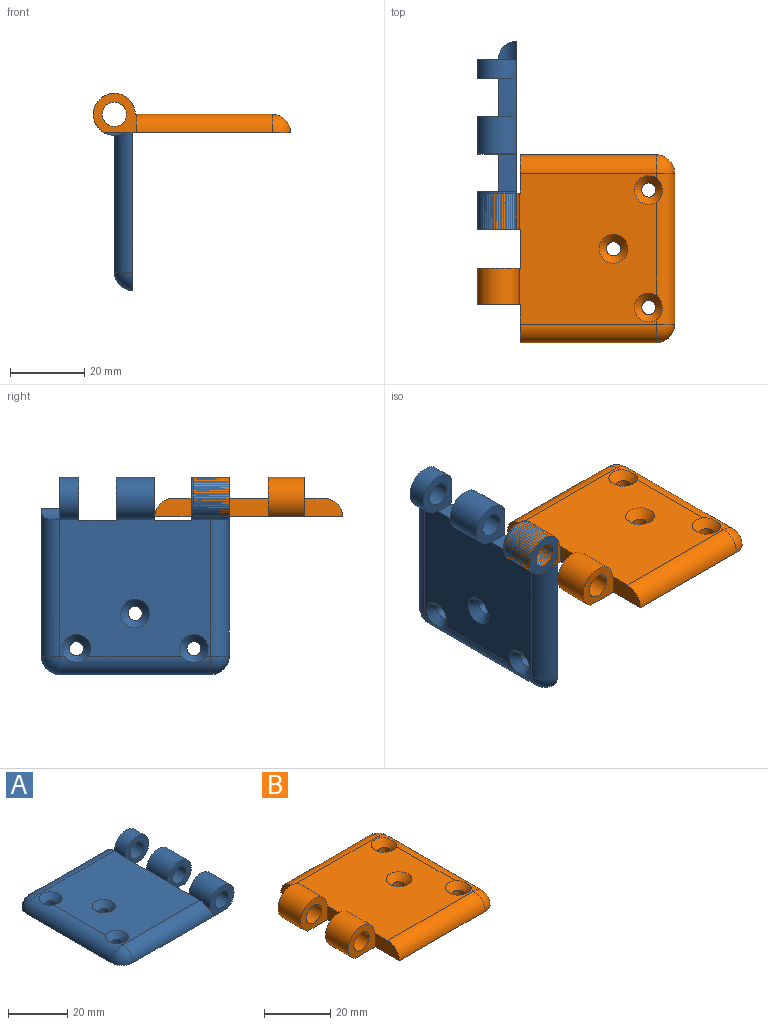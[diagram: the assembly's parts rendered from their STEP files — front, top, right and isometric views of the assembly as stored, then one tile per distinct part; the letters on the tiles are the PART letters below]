
ASSEMBLY  parts=2 mates=1
PART A: 28 faces, bbox 53.3x50.8x10.7 mm
  f0: plane 50.8x50.31mm, normal (0,0,-1), area 2310.2mm2, adj f1,f2,f4,f7,f8,f9,f10,f12
  f1: cylinder r=5.68mm len=11.35mm, axis (0,1,0), area 243.3mm2, adj f0,f5,f9,f14
  f2: cylinder r=5.68mm len=11.35mm, axis (0,1,0), area 123.6mm2, adj f0,f5,f10,f27
  f3: cylinder r=3.28mm len=6.55mm, axis (0,1,0), area 106.2mm2, adj f10,f27
  f4: cylinder r=5.68mm len=11.35mm, axis (0,1,0), area 248.9mm2, adj f0,f5,f7,f13,f21
  f5: plane 40.8x36.95mm, normal (0,0,1), area 1378.2mm2, adj f1,f2,f4,f8,f9,f10,f12,f13
  f6: cylinder r=3.28mm len=10.16mm, axis (0,1,0), area 209.1mm2, adj f7,f13
  f7: plane 11.35x10.68mm, normal (0,-1,0), area 65mm2, adj f0,f4,f6
  f8: plane 10.16x5mm, normal (1,0,0), area 50.8mm2, adj f0,f5,f9,f10
  f9: plane 11.55x10.68mm, normal (0,1,0), area 70.3mm2, adj f0,f1,f5,f8,f11
  f10: plane 11.55x10.68mm, normal (0,-1,0), area 70.3mm2, adj f0,f2,f3,f5,f8
  f11: cylinder r=3.28mm len=10.16mm, axis (0,1,0), area 209.1mm2, adj f9,f14
  f12: plane 10.16x5mm, normal (1,0,0), area 50.8mm2, adj f0,f5,f13,f14
  f13: plane 11.55x10.68mm, normal (0,1,0), area 70.3mm2, adj f0,f4,f5,f6,f12
  f14: plane 11.55x10.68mm, normal (0,-1,0), area 70.3mm2, adj f0,f1,f5,f11,f12
  f15: cylinder r=1.9mm len=3.8mm, axis (0,0,1), area 32.2mm2, adj f0,f16
  f16: cone r=1.9mm half-angle=41deg, axis (0,0,1), area 53.9mm2, adj f5,f15,f25
  f17: cylinder r=1.9mm len=3.8mm, axis (0,0,1), area 32.2mm2, adj f0,f18
  f18: cone r=1.9mm half-angle=41deg, axis (0,0,1), area 55.5mm2, adj f5,f17
  f19: cylinder r=1.9mm len=3.8mm, axis (0,0,1), area 32.2mm2, adj f0,f20
  f20: cone r=1.9mm half-angle=41deg, axis (0,0,1), area 53.9mm2, adj f5,f19,f25
  f21: cylinder r=5mm len=39.94mm, axis (1,0,0), area 294.8mm2, adj f0,f4,f5,f23
  f22: cylinder r=5mm len=39.94mm, axis (-1,0,0), area 294.8mm2, adj f0,f5,f24,f26
  f23: sphere r=5mm, area 39.3mm2, adj f0,f21,f25
  f24: sphere r=5mm, area 39.3mm2, adj f0,f22,f25
  f25: cylinder r=5mm len=40.8mm, axis (0,-1,0), area 304.3mm2, adj f0,f5,f16,f20,f23,f24
  f26: cylinder r=5.68mm len=5mm, axis (0,1,0), area 25mm2, adj f0,f22,f27
  f27: plane 11.35x10.68mm, normal (0,1,0), area 65mm2, adj f0,f2,f3,f26
PART B: 24 faces, bbox 53.3x50.8x10.7 mm
  f0: plane 50.8x50.31mm, normal (0,0,-1), area 2243.3mm2, adj f1,f2,f4,f5,f6,f8,f9,f10
  f1: cylinder r=5.68mm len=11.35mm, axis (0,1,0), area 233.7mm2, adj f0,f3,f4,f8
  f2: cylinder r=5.68mm len=11.35mm, axis (0,1,0), area 233.7mm2, adj f0,f3,f5,f10
  f3: plane 40.8x36.95mm, normal (0,0,1), area 1378mm2, adj f1,f2,f4,f5,f6,f8,f9,f10
  f4: plane 11.55x10.68mm, normal (0,1,0), area 70.3mm2, adj f0,f1,f3,f6,f7
  f5: plane 11.55x10.68mm, normal (0,-1,0), area 70.3mm2, adj f0,f2,f3,f6,f12
  f6: plane 10.56x5mm, normal (-1,0,0), area 52.8mm2, adj f0,f3,f4,f5
  f7: cylinder r=3.28mm len=9.76mm, axis (0,1,0), area 200.8mm2, adj f4,f8
  f8: plane 11.55x10.68mm, normal (0,-1,0), area 70.3mm2, adj f0,f1,f3,f7,f9
  f9: plane 10.36x5mm, normal (-1,0,0), area 46.4mm2, adj f0,f3,f8,f19
  f10: plane 11.55x10.68mm, normal (0,1,0), area 70.3mm2, adj f0,f2,f3,f11,f12
  f11: plane 10.36x5mm, normal (-1,0,0), area 46.4mm2, adj f0,f3,f10,f20
  f12: cylinder r=3.28mm len=9.76mm, axis (0,1,0), area 200.8mm2, adj f5,f10
  f13: cylinder r=1.9mm len=3.8mm, axis (0,0,1), area 32.2mm2, adj f0,f14
  f14: cone r=1.9mm half-angle=41deg, axis (0,0,1), area 53.9mm2, adj f3,f13,f23
  f15: cylinder r=1.9mm len=3.8mm, axis (0,0,1), area 32.2mm2, adj f0,f16
  f16: cone r=1.9mm half-angle=41deg, axis (0,0,1), area 55.5mm2, adj f3,f15
  f17: cylinder r=1.9mm len=3.8mm, axis (0,0,1), area 32.2mm2, adj f0,f18
  f18: cone r=1.9mm half-angle=41deg, axis (0,0,1), area 53.9mm2, adj f3,f17,f23
  f19: cylinder r=5mm len=36.75mm, axis (1,0,0), area 288.6mm2, adj f0,f3,f9,f21
  f20: cylinder r=5mm len=36.75mm, axis (-1,0,0), area 288.6mm2, adj f0,f3,f11,f22
  f21: sphere r=5mm, area 39.3mm2, adj f0,f19,f23
  f22: sphere r=5mm, area 39.3mm2, adj f0,f20,f23
  f23: cylinder r=5mm len=40.8mm, axis (0,1,0), area 304.3mm2, adj f0,f3,f14,f18,f21,f22
PLACE A rot(axis=(0,-1,0),90deg) t=(-24.93,-48.02,21.23)mm
PLACE B t=(-29.93,-78.7,16.23)mm
MATE revolute A.f3 <-> B.f7  axis (0,1,0) through (-29.93,-98.82,21.23)mm
